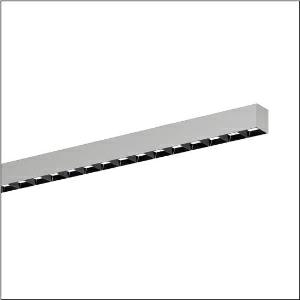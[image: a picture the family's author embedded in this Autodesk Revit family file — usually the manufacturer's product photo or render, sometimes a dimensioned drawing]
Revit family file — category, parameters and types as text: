
# Revit family: silica_r__21_51mx22dc3asb_7d31
name_source: partatom
category: Lighting Fixtures
units: mm (PartAtom-declared; Revit-internal decimal feet)

## family parameters
Cut with Voids When Loaded = No
Host = Face
Light Source = No
Part Type = Normal
Room Calculation Point = No
Round Connector Dimension = Use Diameter
Shared = No

## types (1)
- --- (1 x LED, 10800 lm, 69.2 W, 3000K)
    Apparent Load = 69 VA
    CIE Flux Codes = 86 100 100 100 100
    Color Rendering = 80
    Color Temperature = 3000K
    Default Elevation = 1800 mm
    Description = Silica® 21, office luminaire, primary light control with darklight reflector, of PMMA, black, CAT 2 (L<= 3000cd/m²), light emission: direct distribution, primary light characteristic: symmetric, installation type: surface-mounted, LED, rated luminous flux: 10.800lm, luminous efficacy: 156lm/W, light colour: 830, colour temperature: 3000K, with terminal, 3+2-pole, max. 2.5mm², mains connection: 220..240V, AC, 50/60Hz, rated input power: 69.2W, luminaire housing, of aluminium, metallic grey (RAL 9006), length: 3.004mm, width: 53mm, height: 53mm, protection rating (complete): IP20, insulation class (complete): insulation class I (protective earthing), certification: CE, permissible operating ambient temperature: 0..+35°C, standard: EN 50419, packaging unit: 1 piece
    Height = 0 mm  [stored 0 ft]
    Lamp = 1 x LED
    Lamp Light Flux = 10800 lm
    Lamp Power = 69.2 W
    Lamp count = 1
    Length = 3004 mm
    Luminous efficacy = 156 lm/W
    Manufacturer = Siteco
    ModVariant = No
    Model = 51MX22DC3ASB
    Mounting Place = Ceiling
    Mounting Type = Recessed
    Number of Poles = 1
    OnlyDefault = Yes
    Power Factor = 1
    Product Name = Silica® 21
    Product group = office luminaire | ceiling recessed
    ProductGroupID = 401
    Protection Class = Protection class I
    Protection Degree = IP 20
    RLX_Detail_Level = 1
    RLX_Emergency_Light_Flux = 0 lm
    RLX_Emergency_Type = 0
    RLX_Emergency_Type_DB = No
    RlxData = <blob elided: 62901 chars, md5=2afe6618>
    Socket = socket
    Standby Power = 0 W
    System Light Flux = 10800 lm
    System Power = 69 W
    Type Comments = factory setting: luminous flux: 100 % | dim-lin: 254 | 392 mA
    Type Image = l_1297764.jpg
    URL = http://relux.com
    VarID = @adj_055787
    Voltage = 0 V
    Weight = 0.00 kg
    Width = 53 mm

note: [stored X ft] marks values corroborated as IEEE doubles in the binary element streams (Revit-internal decimal feet)

## geometry (parser evidence)
native form markers: Blend x4, Sweep x10
no freeform markers — native parametric forms only
